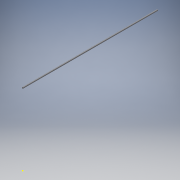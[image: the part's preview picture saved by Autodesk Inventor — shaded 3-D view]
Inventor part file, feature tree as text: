
AUTODESK INVENTOR PART (.ipt)
format: ipt  version: 2017 (Build 210142000, 142)  size: 91,648 bytes
history: native  units: mm
features: sketch x2, extrude x1, thread x1
ambient origin geometry x8: Origin, YZ Plane, XZ Plane, XY Plane, X Axis, Y Axis, Z Axis, Center Point
bodies: Solid1 (feature_tree)
feature tree (4):
  sketch  "Sketch1"  dims[d0=8.0mm d1=800.0mm d2=0.0mm d3=10.0mm d4=0.0mm]
  extrude  "Extrusion1"  Depth=800.0mm TaperAngle=0.0deg
  thread  "Thread1"  [1 undecoded]
  sketch  "Sketch2"
note: 1 required parameter value undecoded (feature->parameter linkage not recoverable at this tier; creation-order binding heuristic only, values carry confidence <= 0.55)
